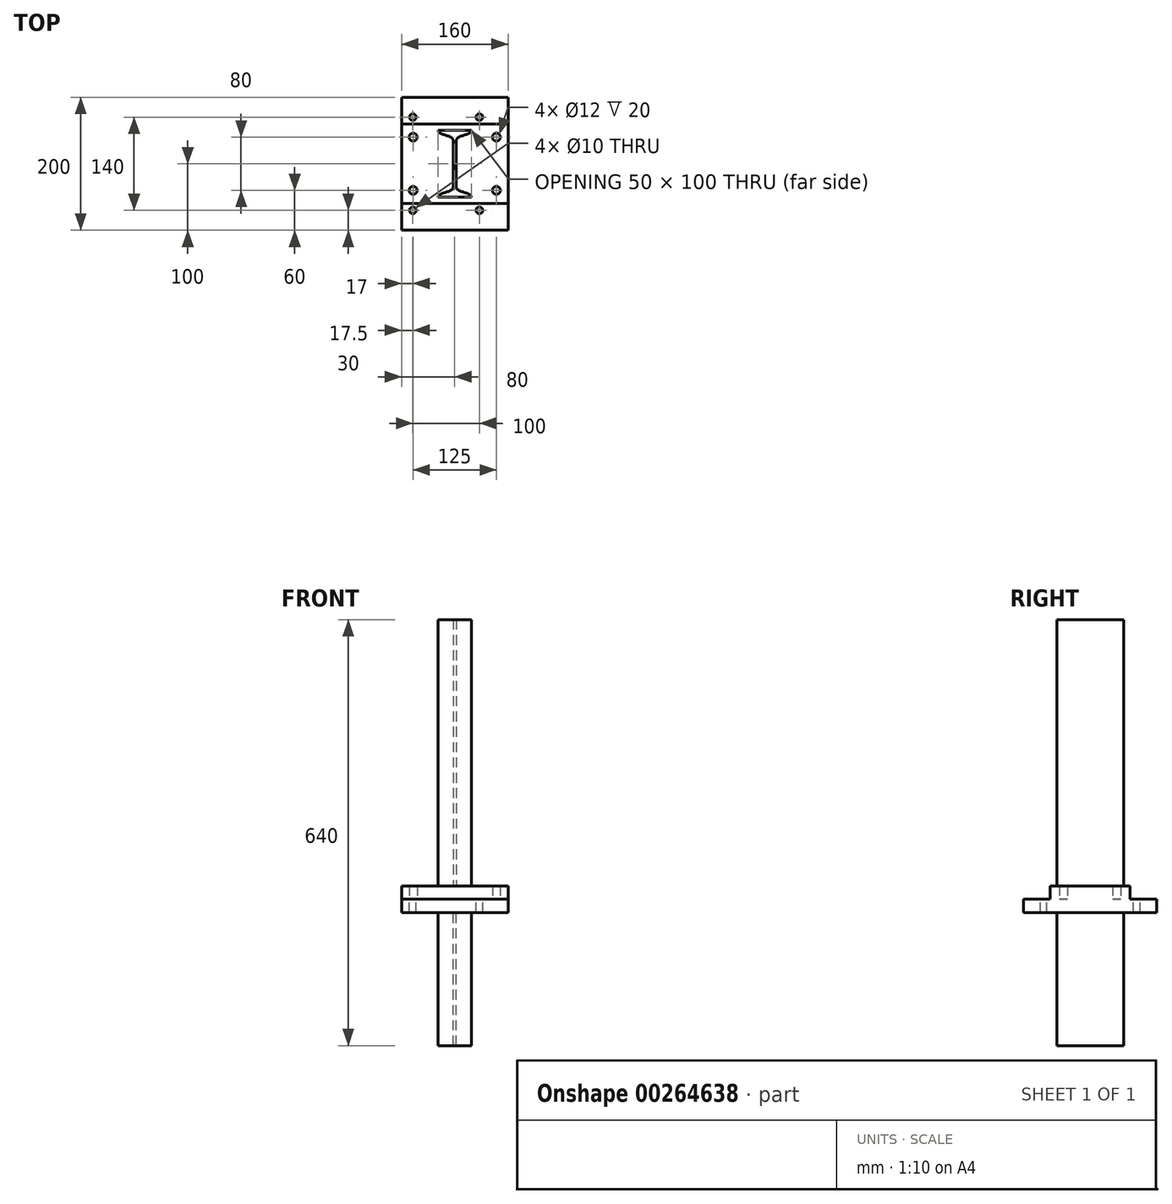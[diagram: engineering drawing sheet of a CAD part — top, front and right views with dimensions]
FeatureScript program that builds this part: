
annotation { "Feature Type Name" : "Feature", "Feature Type Description" : "" }
export const myFeature = defineFeature(function(context is Context, id is Id, definition is map)
    precondition{}
    {
        {
            var Q0;
            Q0=qCreatedBy(makeId("Top.planeOp"),FACE);
            var sketch = newSketch(context, id + "F0", { "sketchPlane" : qUnion([Q0])});
            skLineSegment(sketch, "E0.bottom", {"start": v(-80, 60) * mm, "end": v(80, 60) * mm});
            skLineSegment(sketch, "E0.top", {"start": v(-80, -60) * mm, "end": v(80, -60) * mm});
            skLineSegment(sketch, "E0.left", {"start": v(-80, 60) * mm, "end": v(-80, -60) * mm});
            skLineSegment(sketch, "E0.right", {"start": v(80, 60) * mm, "end": v(80, -60) * mm});
            skPoint(sketch, "E0.middle", {"position": v(0, 0) * mm});
            skLineSegment(sketch, "E1.bottom", {"start": v(-62.5, 40) * mm, "end": v(62.5, 40) * mm, "construction": true});
            skLineSegment(sketch, "E1.top", {"start": v(-62.5, -40) * mm, "end": v(62.5, -40) * mm, "construction": true});
            skLineSegment(sketch, "E1.left", {"start": v(-62.5, 40) * mm, "end": v(-62.5, -40) * mm, "construction": true});
            skLineSegment(sketch, "E1.right", {"start": v(62.5, 40) * mm, "end": v(62.5, -40) * mm, "construction": true});
            skCircle(sketch, "E2", {"center": v(-62.5, -40) * mm, "radius": 6 * mm});
            skCircle(sketch, "E3", {"center": v(-62.5, 40) * mm, "radius": 6 * mm});
            skCircle(sketch, "E4", {"center": v(62.5, 40) * mm, "radius": 6 * mm});
            skCircle(sketch, "E5", {"center": v(62.5, -40) * mm, "radius": 6 * mm});
            skLineSegment(sketch, "E6.bottom", {"start": v(-25, 50) * mm, "end": v(25, 50) * mm});
            skLineSegment(sketch, "E6.top", {"start": v(-25, -50) * mm, "end": v(25, -50) * mm});
            skLineSegment(sketch, "E6.left", {"start": v(-25, 50) * mm, "end": v(-25, -50) * mm, "construction": true});
            skLineSegment(sketch, "E6.right", {"start": v(25, 50) * mm, "end": v(25, -50) * mm, "construction": true});
            skLineSegment(sketch, "E7.bottom", {"start": v(-2.5, 35.38) * mm, "end": v(2.5, 35.38) * mm, "construction": true});
            skLineSegment(sketch, "E7.top", {"start": v(-2.5, -35.38) * mm, "end": v(2.5, -35.38) * mm, "construction": true});
            skLineSegment(sketch, "E7.left", {"start": v(-2.5, 35.38) * mm, "end": v(-2.5, -35.38) * mm});
            skLineSegment(sketch, "E7.right", {"start": v(2.5, 35.38) * mm, "end": v(2.5, -35.38) * mm});
            skFitSpline(sketch, "E8", {"points": [v(-25, 50) * mm, v(-2.5, 35.38) * mm], "startDerivative": vector(0, -21) * mm, "endDerivative": vector(0, -22.87) * mm});
            skFitSpline(sketch, "E9", {"points": [v(2.5, 35.38) * mm, v(25, 50) * mm], "startDerivative": vector(0, 22.87) * mm, "endDerivative": vector(0, 21) * mm});
            skFitSpline(sketch, "E10", {"points": [v(-25, -50) * mm, v(-2.5, -35.38) * mm], "startDerivative": vector(0, 21) * mm, "endDerivative": vector(0, 22.88) * mm});
            skFitSpline(sketch, "E11", {"points": [v(25, -50) * mm, v(2.5, -35.38) * mm], "startDerivative": vector(0, 21) * mm, "endDerivative": vector(0, 22.87) * mm});
            skSolve(sketch);
        }
        {
            var Q0;
            Q0=makeQuery(id+"F0.imprint","IMPRINT",FACE,{"disambiguationData":[TD([[makeQuery(id+"F0.imprint","IMPRINT",EDGE,{"derivedFrom":sQuery(id+"F0.wireOp",EDGE,"E6.bottom")}),-1.0]])]});
            extrude(context, id + "F1", {"entities" : qUnion([Q0]), "depth" : 420 * mm});
        }
        {
            var Q0;
            Q0=makeQuery(id+"F0.imprint","IMPRINT",FACE,{"disambiguationData":[TD([[makeQuery(id+"F0.imprint","IMPRINT",EDGE,{"derivedFrom":sQuery(id+"F0.wireOp",EDGE,"E0.bottom")}),-1.0]])]});
            var Q1;
            Q1=makeQuery(id+"F0.imprint","IMPRINT",FACE,{"disambiguationData":[TD([[makeQuery(id+"F0.imprint","IMPRINT",EDGE,{"derivedFrom":sQuery(id+"F0.wireOp",EDGE,"E6.bottom")}),-1.0]])]});
            extrude(context, id + "F2", {"entities" : qUnion([Q0, Q1]), "operationType" : NewBodyOperationType.ADD, "depth" : 20 * mm});
        }
        {
            var Q0;
            Q0=makeQuery(id+"F0.imprint","IMPRINT",FACE,{"disambiguationData":[TD([[makeQuery(id+"F0.imprint","IMPRINT",EDGE,{"derivedFrom":sQuery(id+"F0.wireOp",EDGE,"E6.bottom")}),-1.0]])]});
            extrude(context, id + "F3", {"entities" : qUnion([Q0]), "oppositeDirection" : true, "depth" : 220 * mm});
        }
        {
            var Q0;
            Q0=qCreatedBy(makeId("Top.planeOp"),FACE);
            var sketch = newSketch(context, id + "F4", { "sketchPlane" : qUnion([Q0])});
            skLineSegment(sketch, "E12.bottom", {"start": v(-80, -100) * mm, "end": v(80, -100) * mm});
            skLineSegment(sketch, "E12.top", {"start": v(-80, 100) * mm, "end": v(80, 100) * mm});
            skLineSegment(sketch, "E12.left", {"start": v(-80, -100) * mm, "end": v(-80, 100) * mm});
            skLineSegment(sketch, "E12.right", {"start": v(80, -100) * mm, "end": v(80, 100) * mm});
            skPoint(sketch, "E12.middle", {"position": v(0, 0) * mm});
            skLineSegment(sketch, "E13.bottom", {"start": v(-63, -70) * mm, "end": v(37, -70) * mm, "construction": true});
            skLineSegment(sketch, "E13.top", {"start": v(-63, 70) * mm, "end": v(37, 70) * mm, "construction": true});
            skLineSegment(sketch, "E13.left", {"start": v(-63, -70) * mm, "end": v(-63, 70) * mm, "construction": true});
            skLineSegment(sketch, "E13.right", {"start": v(37, -70) * mm, "end": v(37, 70) * mm, "construction": true});
            skCircle(sketch, "E14", {"center": v(-63, 70) * mm, "radius": 5 * mm});
            skCircle(sketch, "E15", {"center": v(37, 70) * mm, "radius": 5 * mm});
            skCircle(sketch, "E16", {"center": v(37, -70) * mm, "radius": 5 * mm});
            skCircle(sketch, "E17", {"center": v(-63, -70) * mm, "radius": 5 * mm});
            skSolve(sketch);
        }
        {
            var Q0;
            Q0=makeQuery(id+"F4.imprint","IMPRINT",FACE,{"disambiguationData":[TD([[makeQuery(id+"F4.imprint","IMPRINT",EDGE,{"derivedFrom":sQuery(id+"F4.wireOp",EDGE,"E12.bottom")}),1.0]])]});
            extrude(context, id + "F5", {"entities" : qUnion([Q0]), "operationType" : NewBodyOperationType.ADD, "oppositeDirection" : true, "depth" : 20 * mm});
        }
    });
